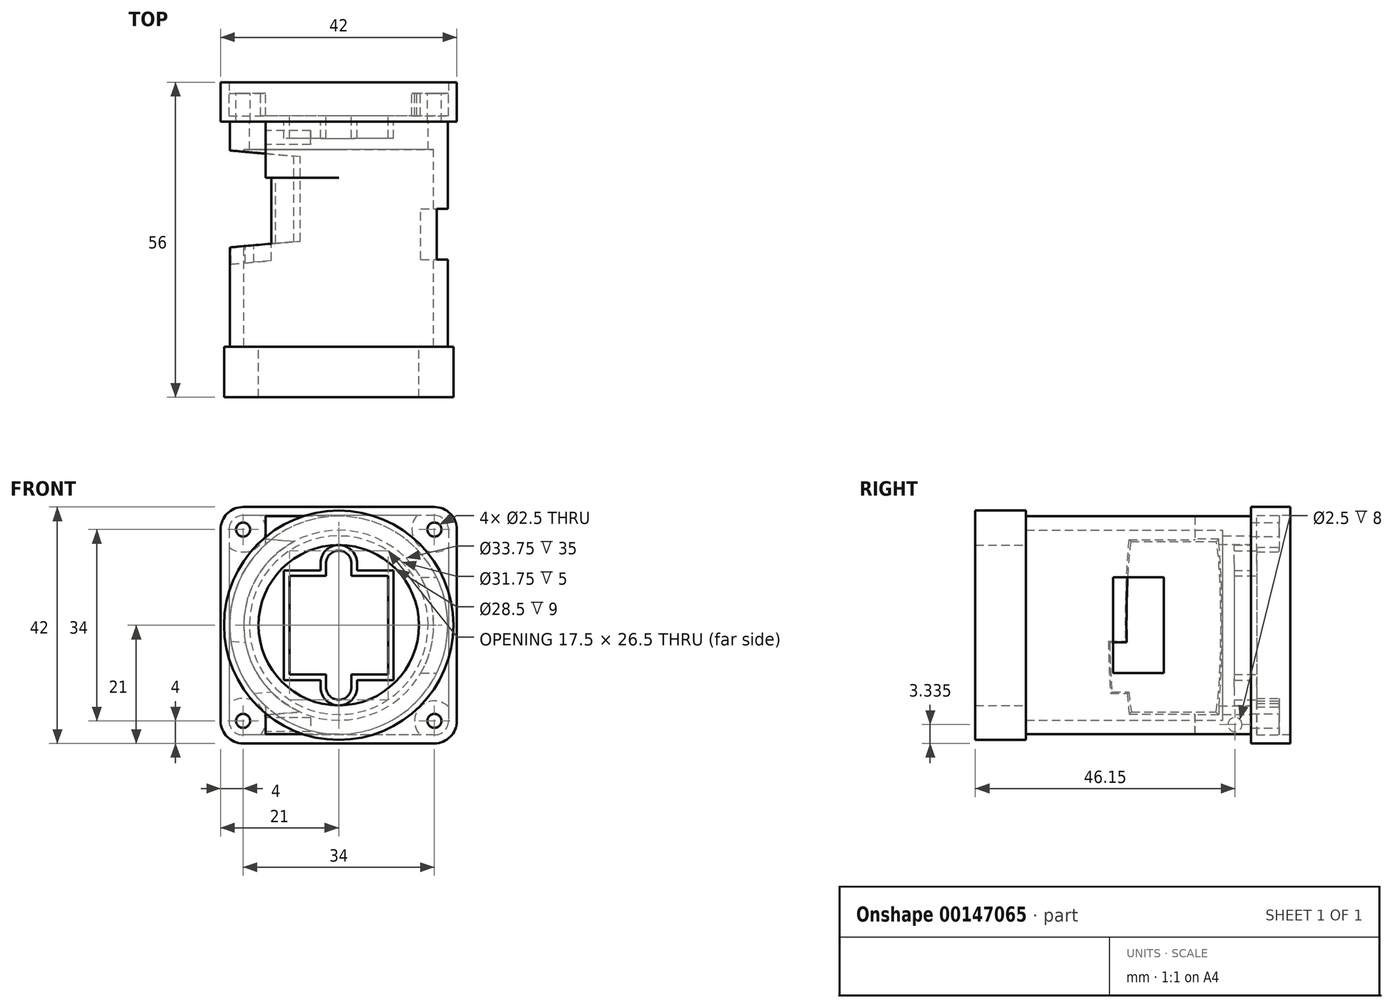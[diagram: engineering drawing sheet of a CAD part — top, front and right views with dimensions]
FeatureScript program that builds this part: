
annotation { "Feature Type Name" : "Feature", "Feature Type Description" : "" }
export const myFeature = defineFeature(function(context is Context, id is Id, definition is map)
    precondition{}
    {
        {
            var Q0;
            Q0=qCreatedBy(makeId("Front.planeOp"),FACE);
            var sketch = newSketch(context, id + "F0", { "sketchPlane" : qUnion([Q0])});
            skLineSegment(sketch, "E0.bottom", {"start": v(17, 19.5) * mm, "end": v(-17, 19.5) * mm});
            skLineSegment(sketch, "E0.top", {"start": v(17, -19.5) * mm, "end": v(-17, -19.5) * mm});
            skLineSegment(sketch, "E0.left", {"start": v(19.5, 17) * mm, "end": v(19.5, -17) * mm});
            skLineSegment(sketch, "E0.right", {"start": v(-19.5, 17) * mm, "end": v(-19.5, -17) * mm});
            skPoint(sketch, "E0.middle", {"position": v(0, 0) * mm});
            skPoint(sketch, "E1.visualSharp", {"position": v(-19.5, 19.5) * mm});
            skArc(sketch, "E1.filletArc", {"start": v(-17, 19.5) * mm, "mid": v(-18.77, 18.77) * mm, "end": v(-19.5, 17) * mm});
            skPoint(sketch, "E2.visualSharp", {"position": v(19.5, 19.5) * mm});
            skArc(sketch, "E2.filletArc", {"start": v(19.5, 17) * mm, "mid": v(18.77, 18.77) * mm, "end": v(17, 19.5) * mm});
            skPoint(sketch, "E3.visualSharp", {"position": v(19.5, -19.5) * mm});
            skArc(sketch, "E3.filletArc", {"start": v(17, -19.5) * mm, "mid": v(18.77, -18.77) * mm, "end": v(19.5, -17) * mm});
            skPoint(sketch, "E4.visualSharp", {"position": v(-19.5, -19.5) * mm});
            skArc(sketch, "E4.filletArc", {"start": v(-19.5, -17) * mm, "mid": v(-18.77, -18.77) * mm, "end": v(-17, -19.5) * mm});
            skLineSegment(sketch, "E5.0", {"start": v(17, 21) * mm, "end": v(-17, 21) * mm});
            skArc(sketch, "E5.1", {"start": v(21, 17) * mm, "mid": v(19.83, 19.83) * mm, "end": v(17, 21) * mm});
            skArc(sketch, "E5.2", {"start": v(-17, 21) * mm, "mid": v(-19.83, 19.83) * mm, "end": v(-21, 17) * mm});
            skLineSegment(sketch, "E5.3", {"start": v(21, 17) * mm, "end": v(21, -17) * mm});
            skLineSegment(sketch, "E5.4", {"start": v(-21, 17) * mm, "end": v(-21, -17) * mm});
            skArc(sketch, "E5.5", {"start": v(-21, -17) * mm, "mid": v(-19.83, -19.83) * mm, "end": v(-17, -21) * mm});
            skLineSegment(sketch, "E5.6", {"start": v(17, -21) * mm, "end": v(-17, -21) * mm});
            skArc(sketch, "E5.7", {"start": v(17, -21) * mm, "mid": v(19.83, -19.83) * mm, "end": v(21, -17) * mm});
            skCircle(sketch, "E6", {"center": v(-17, 17) * mm, "radius": 1.25 * mm});
            skLineSegment(sketch, "E7", {"start": v(0, 21) * mm, "end": v(0, -21) * mm, "construction": true});
            skLineSegment(sketch, "E8", {"start": v(-21, 0) * mm, "end": v(21, 0) * mm, "construction": true});
            skCircle(sketch, "E9", {"center": v(17, 17) * mm, "radius": 1.25 * mm});
            skCircle(sketch, "E10", {"center": v(17, -17) * mm, "radius": 1.25 * mm});
            skCircle(sketch, "E11", {"center": v(-17, -17) * mm, "radius": 1.25 * mm});
            skCircle(sketch, "E12", {"center": v(-17, 17) * mm, "radius": 4 * mm});
            skCircle(sketch, "E13", {"center": v(17, 17) * mm, "radius": 4 * mm});
            skCircle(sketch, "E14", {"center": v(17, -17) * mm, "radius": 3.54 * mm});
            skCircle(sketch, "E15", {"center": v(-17, -17) * mm, "radius": 4 * mm});
            skSolve(sketch);
        }
        {
            var Q0;
            {var subQ0=sQuery(id+"F0.wireOp",EDGE,"E1.filletArc");Q0=makeQuery(id+"F0.imprint","IMPRINT",FACE,{"disambiguationData":[TD([[makeQuery(id+"F0.imprint","IMPRINT",EDGE,{"derivedFrom":subQ0}),1.0]])]});}
            var Q1;
            {var subQ0=sQuery(id+"F0.wireOp",EDGE,"E2.filletArc");Q1=makeQuery(id+"F0.imprint","IMPRINT",FACE,{"disambiguationData":[TD([[makeQuery(id+"F0.imprint","IMPRINT",EDGE,{"derivedFrom":subQ0}),1.0]])]});}
            var Q2;
            {var subQ0=sQuery(id+"F0.wireOp",EDGE,"E3.filletArc");Q2=makeQuery(id+"F0.imprint","IMPRINT",FACE,{"disambiguationData":[TD([[makeQuery(id+"F0.imprint","IMPRINT",EDGE,{"derivedFrom":subQ0}),1.0]])]});}
            var Q3;
            {var subQ0=sQuery(id+"F0.wireOp",EDGE,"E4.filletArc");Q3=makeQuery(id+"F0.imprint","IMPRINT",FACE,{"disambiguationData":[TD([[makeQuery(id+"F0.imprint","IMPRINT",EDGE,{"derivedFrom":subQ0}),1.0]])]});}
            var Q4;
            {var subQ5=sQuery(id+"F0.wireOp",EDGE,"E5.4");Q4=makeQuery(id+"F0.imprint","IMPRINT",FACE,{"disambiguationData":[TD([[makeQuery(id+"F0.imprint","IMPRINT",EDGE,{"derivedFrom":subQ5}),1.0]])]});}
            var Q5;
            {var subQ0=sQuery(id+"F0.wireOp",EDGE,"E14");var subQ1=sQuery(id+"F0.wireOp",EDGE,"E0.top");var subQ2=makeQuery(id+"F0.imprint","INTERSECT",VERTEX,{"derivedFrom":[subQ1,subQ0]});Q5=makeQuery(id+"F0.imprint","IMPRINT",FACE,{"disambiguationData":[TD([[makeQuery(id+"F0.imprint","IMPRINT",EDGE,{"disambiguationData":[TD([[subQ2,-1.0]])],"derivedFrom":subQ1}),1.0]])]});}
            var Q6;
            {var subQ4=sQuery(id+"F0.wireOp",EDGE,"E1.filletArc");Q6=makeQuery(id+"F0.imprint","IMPRINT",FACE,{"disambiguationData":[TD([[makeQuery(id+"F0.imprint","IMPRINT",EDGE,{"derivedFrom":subQ4}),-1.0]])]});}
            var Q7;
            {var subQ5=sQuery(id+"F0.wireOp",EDGE,"E5.0");Q7=makeQuery(id+"F0.imprint","IMPRINT",FACE,{"disambiguationData":[TD([[makeQuery(id+"F0.imprint","IMPRINT",EDGE,{"derivedFrom":subQ5}),1.0]])]});}
            var Q8;
            {var subQ3=sQuery(id+"F0.wireOp",EDGE,"E2.filletArc");Q8=makeQuery(id+"F0.imprint","IMPRINT",FACE,{"disambiguationData":[TD([[makeQuery(id+"F0.imprint","IMPRINT",EDGE,{"derivedFrom":subQ3}),-1.0]])]});}
            var Q9;
            {var subQ0=sQuery(id+"F0.wireOp",EDGE,"E13");var subQ1=sQuery(id+"F0.wireOp",EDGE,"E0.left");var subQ2=makeQuery(id+"F0.imprint","INTERSECT",VERTEX,{"derivedFrom":[subQ1,subQ0]});Q9=makeQuery(id+"F0.imprint","IMPRINT",FACE,{"disambiguationData":[TD([[makeQuery(id+"F0.imprint","IMPRINT",EDGE,{"disambiguationData":[TD([[subQ2,-1.0]])],"derivedFrom":subQ1}),1.0]])]});}
            var Q10;
            {var subQ0=sQuery(id+"F0.wireOp",EDGE,"E3.filletArc");Q10=makeQuery(id+"F0.imprint","IMPRINT",FACE,{"disambiguationData":[TD([[makeQuery(id+"F0.imprint","IMPRINT",EDGE,{"derivedFrom":subQ0}),-1.0]])]});}
            var Q11;
            {var subQ4=sQuery(id+"F0.wireOp",EDGE,"E4.filletArc");Q11=makeQuery(id+"F0.imprint","IMPRINT",FACE,{"disambiguationData":[TD([[makeQuery(id+"F0.imprint","IMPRINT",EDGE,{"derivedFrom":subQ4}),-1.0]])]});}
            extrude(context, id + "F1", {"entities" : qUnion([Q0, Q1, Q2, Q3, Q4, Q5, Q6, Q7, Q8, Q9, Q10, Q11]), "depth" : 4 * mm});
        }
        {
            var Q0;
            {var subQ5=sQuery(id+"F0.wireOp",EDGE,"E5.0");Q0=makeQuery(id+"F0.imprint","IMPRINT",FACE,{"disambiguationData":[TD([[makeQuery(id+"F0.imprint","IMPRINT",EDGE,{"derivedFrom":subQ5}),1.0]])]});}
            var Q1;
            {var subQ3=sQuery(id+"F0.wireOp",EDGE,"E2.filletArc");Q1=makeQuery(id+"F0.imprint","IMPRINT",FACE,{"disambiguationData":[TD([[makeQuery(id+"F0.imprint","IMPRINT",EDGE,{"derivedFrom":subQ3}),-1.0]])]});}
            var Q2;
            {var subQ4=sQuery(id+"F0.wireOp",EDGE,"E1.filletArc");Q2=makeQuery(id+"F0.imprint","IMPRINT",FACE,{"disambiguationData":[TD([[makeQuery(id+"F0.imprint","IMPRINT",EDGE,{"derivedFrom":subQ4}),-1.0]])]});}
            var Q3;
            {var subQ5=sQuery(id+"F0.wireOp",EDGE,"E5.4");Q3=makeQuery(id+"F0.imprint","IMPRINT",FACE,{"disambiguationData":[TD([[makeQuery(id+"F0.imprint","IMPRINT",EDGE,{"derivedFrom":subQ5}),1.0]])]});}
            var Q4;
            {var subQ4=sQuery(id+"F0.wireOp",EDGE,"E4.filletArc");Q4=makeQuery(id+"F0.imprint","IMPRINT",FACE,{"disambiguationData":[TD([[makeQuery(id+"F0.imprint","IMPRINT",EDGE,{"derivedFrom":subQ4}),-1.0]])]});}
            var Q5;
            {var subQ0=sQuery(id+"F0.wireOp",EDGE,"E14");var subQ1=sQuery(id+"F0.wireOp",EDGE,"E0.top");var subQ2=makeQuery(id+"F0.imprint","INTERSECT",VERTEX,{"derivedFrom":[subQ1,subQ0]});Q5=makeQuery(id+"F0.imprint","IMPRINT",FACE,{"disambiguationData":[TD([[makeQuery(id+"F0.imprint","IMPRINT",EDGE,{"disambiguationData":[TD([[subQ2,-1.0]])],"derivedFrom":subQ1}),1.0]])]});}
            var Q6;
            {var subQ0=sQuery(id+"F0.wireOp",EDGE,"E3.filletArc");Q6=makeQuery(id+"F0.imprint","IMPRINT",FACE,{"disambiguationData":[TD([[makeQuery(id+"F0.imprint","IMPRINT",EDGE,{"derivedFrom":subQ0}),-1.0]])]});}
            var Q7;
            {var subQ0=sQuery(id+"F0.wireOp",EDGE,"E13");var subQ1=sQuery(id+"F0.wireOp",EDGE,"E0.left");var subQ2=makeQuery(id+"F0.imprint","INTERSECT",VERTEX,{"derivedFrom":[subQ1,subQ0]});Q7=makeQuery(id+"F0.imprint","IMPRINT",FACE,{"disambiguationData":[TD([[makeQuery(id+"F0.imprint","IMPRINT",EDGE,{"disambiguationData":[TD([[subQ2,-1.0]])],"derivedFrom":subQ1}),1.0]])]});}
            extrude(context, id + "F2", {"entities" : qUnion([Q0, Q1, Q2, Q3, Q4, Q5, Q6, Q7]), "operationType" : NewBodyOperationType.ADD, "oppositeDirection" : true, "depth" : 2 * mm});
        }
        {
            var Q0;
            Q0=makeQuery(id+"F1.opExtrude","CAP_FACE",FACE,{"disambiguationData":[OSD([sQuery(id+"F0.wireOp",EDGE,"E0.bottom"),sQuery(id+"F0.wireOp",EDGE,"E0.top"),sQuery(id+"F0.wireOp",EDGE,"E0.left"),sQuery(id+"F0.wireOp",EDGE,"E0.right"),sQuery(id+"F0.wireOp",EDGE,"E5.0"),sQuery(id+"F0.wireOp",EDGE,"E5.3"),sQuery(id+"F0.wireOp",EDGE,"E5.4"),sQuery(id+"F0.wireOp",EDGE,"E5.6"),sQuery(id+"F0.wireOp",EDGE,"E5.7"),sQuery(id+"F0.wireOp",EDGE,"E6"),sQuery(id+"F0.wireOp",EDGE,"E9"),sQuery(id+"F0.wireOp",EDGE,"E10"),sQuery(id+"F0.wireOp",EDGE,"E11"),sQuery(id+"F0.wireOp",EDGE,"E12"),sQuery(id+"F0.wireOp",EDGE,"E13"),sQuery(id+"F0.wireOp",EDGE,"E14"),sQuery(id+"F0.wireOp",EDGE,"E15")])],"isStart":false});
            var sketch = newSketch(context, id + "F3", { "sketchPlane" : qUnion([Q0])});
            skArc(sketch, "E16.0", {"start": v(-17, 21) * mm, "mid": v(-19.83, 19.83) * mm, "end": v(-21, 17) * mm});
            skLineSegment(sketch, "E16.1", {"start": v(17, 21) * mm, "end": v(-17, 21) * mm});
            skLineSegment(sketch, "E16.2", {"start": v(-21, 17) * mm, "end": v(-21, -17) * mm});
            skArc(sketch, "E16.3", {"start": v(-21, -17) * mm, "mid": v(-19.83, -19.83) * mm, "end": v(-17, -21) * mm});
            skLineSegment(sketch, "E16.4", {"start": v(17, -21) * mm, "end": v(-17, -21) * mm});
            skArc(sketch, "E16.5", {"start": v(17, -21) * mm, "mid": v(19.83, -19.83) * mm, "end": v(21, -17) * mm});
            skLineSegment(sketch, "E16.6", {"start": v(21, 17) * mm, "end": v(21, -17) * mm});
            skArc(sketch, "E16.7", {"start": v(21, 17) * mm, "mid": v(19.83, 19.83) * mm, "end": v(17, 21) * mm});
            skLineSegment(sketch, "E17.0", {"start": v(-21, 0) * mm, "end": v(21, 0) * mm, "construction": true});
            skLineSegment(sketch, "E17.1", {"start": v(0, 21) * mm, "end": v(0, -21) * mm, "construction": true});
            skLineSegment(sketch, "E18.bottom", {"start": v(8.75, 8.75) * mm, "end": v(2.25, 8.75) * mm});
            skLineSegment(sketch, "E18.top", {"start": v(8.75, -8.75) * mm, "end": v(2.25, -8.75) * mm});
            skLineSegment(sketch, "E18.left", {"start": v(8.75, 8.75) * mm, "end": v(8.75, -8.75) * mm});
            skLineSegment(sketch, "E18.right", {"start": v(-8.75, 8.75) * mm, "end": v(-8.75, -8.75) * mm});
            skPoint(sketch, "E18.middle", {"position": v(0, 0) * mm});
            skLineSegment(sketch, "E19.0", {"start": v(11, 11) * mm, "end": v(-11, 11) * mm, "construction": true});
            skLineSegment(sketch, "E19.1", {"start": v(11, 11) * mm, "end": v(11, -11) * mm, "construction": true});
            skLineSegment(sketch, "E19.2", {"start": v(11, -11) * mm, "end": v(-11, -11) * mm, "construction": true});
            skLineSegment(sketch, "E19.3", {"start": v(-11, 11) * mm, "end": v(-11, -11) * mm, "construction": true});
            skArc(sketch, "E20", {"start": v(-2.25, 11) * mm, "mid": v(0, 13.25) * mm, "end": v(2.25, 11) * mm});
            skLineSegment(sketch, "E21", {"start": v(-2.25, 11) * mm, "end": v(-2.25, 8.75) * mm});
            skLineSegment(sketch, "E22", {"start": v(2.25, 11) * mm, "end": v(2.25, 8.75) * mm});
            skLineSegment(sketch, "E23.trimOffspring", {"start": v(-2.25, 8.75) * mm, "end": v(-8.75, 8.75) * mm});
            skLineSegment(sketch, "E24.MirrorCS", {"start": v(-2.25, -11) * mm, "end": v(-2.25, -8.75) * mm});
            skLineSegment(sketch, "E25.MirrorCS", {"start": v(2.25, -11) * mm, "end": v(2.25, -8.75) * mm});
            skArc(sketch, "E26.MirrorCS", {"start": v(-2.25, -11) * mm, "mid": v(0, -13.25) * mm, "end": v(2.25, -11) * mm});
            skLineSegment(sketch, "E27.trimOffspring", {"start": v(-2.25, -8.75) * mm, "end": v(-8.75, -8.75) * mm});
            skArc(sketch, "E28.0", {"start": v(-3.25, -11) * mm, "mid": v(0, -14.25) * mm, "end": v(3.25, -11) * mm});
            skLineSegment(sketch, "E28.1", {"start": v(-3.25, 11) * mm, "end": v(-3.25, 9.75) * mm});
            skLineSegment(sketch, "E28.2", {"start": v(-3.25, 9.75) * mm, "end": v(-9.75, 9.75) * mm});
            skLineSegment(sketch, "E28.3", {"start": v(-9.75, 9.75) * mm, "end": v(-9.75, -9.75) * mm});
            skLineSegment(sketch, "E28.4", {"start": v(-3.25, -9.75) * mm, "end": v(-9.75, -9.75) * mm});
            skArc(sketch, "E28.5", {"start": v(-3.25, 11) * mm, "mid": v(0, 14.25) * mm, "end": v(3.25, 11) * mm});
            skLineSegment(sketch, "E28.6", {"start": v(-3.25, -11) * mm, "end": v(-3.25, -9.75) * mm});
            skLineSegment(sketch, "E28.7", {"start": v(3.25, 11) * mm, "end": v(3.25, 9.75) * mm});
            skLineSegment(sketch, "E28.8", {"start": v(9.75, 9.75) * mm, "end": v(3.25, 9.75) * mm});
            skLineSegment(sketch, "E28.9", {"start": v(9.75, 9.75) * mm, "end": v(9.75, -9.75) * mm});
            skLineSegment(sketch, "E28.10", {"start": v(9.75, -9.75) * mm, "end": v(3.25, -9.75) * mm});
            skLineSegment(sketch, "E28.11", {"start": v(3.25, -11) * mm, "end": v(3.25, -9.75) * mm});
            skSolve(sketch);
        }
        {
            var Q0;
            Q0=makeQuery(id+"F3.imprint","IMPRINT",FACE,{"disambiguationData":[TD([[makeQuery(id+"F3.imprint","IMPRINT",EDGE,{"derivedFrom":sQuery(id+"F3.wireOp",EDGE,"E16.0")}),1.0]])]});
            var Q1;
            Q1=makeQuery(id+"F3.imprint","IMPRINT",FACE,{"disambiguationData":[TD([[makeQuery(id+"F3.imprint","IMPRINT",EDGE,{"derivedFrom":sQuery(id+"F3.wireOp",EDGE,"E28.0")}),-1.0]])]});
            var Q2;
            Q2=makeQuery(id+"F3.imprint","IMPRINT",FACE,{"disambiguationData":[TD([[makeQuery(id+"F3.imprint","IMPRINT",EDGE,{"derivedFrom":sQuery(id+"F3.wireOp",EDGE,"E18.bottom")}),-1.0]])]});
            extrude(context, id + "F4", {"entities" : qUnion([Q0, Q1, Q2]), "operationType" : NewBodyOperationType.ADD, "depth" : 1 * mm, "offsetDistance" : 25 * mm});
        }
        {
            var Q0;
            Q0=makeQuery(id+"F3.imprint","IMPRINT",FACE,{"disambiguationData":[TD([[makeQuery(id+"F3.imprint","IMPRINT",EDGE,{"derivedFrom":sQuery(id+"F3.wireOp",EDGE,"E18.bottom")}),-1.0]])]});
            extrude(context, id + "F5", {"entities" : qUnion([Q0]), "operationType" : NewBodyOperationType.ADD, "depth" : 4 * mm, "offsetDistance" : 25 * mm});
        }
        {
            var Q0;
            Q0=makeQuery(id+"F4.opExtrude","CAP_FACE",FACE,{"disambiguationData":[OSD([sQuery(id+"F0.wireOp",EDGE,"E6"),sQuery(id+"F0.wireOp",EDGE,"E9"),sQuery(id+"F0.wireOp",EDGE,"E10"),sQuery(id+"F0.wireOp",EDGE,"E11"),sQuery(id+"F3.wireOp",EDGE,"E16.0"),sQuery(id+"F3.wireOp",EDGE,"E16.1"),sQuery(id+"F3.wireOp",EDGE,"E16.2"),sQuery(id+"F3.wireOp",EDGE,"E16.3"),sQuery(id+"F3.wireOp",EDGE,"E16.4"),sQuery(id+"F3.wireOp",EDGE,"E16.5"),sQuery(id+"F3.wireOp",EDGE,"E16.6"),sQuery(id+"F3.wireOp",EDGE,"E16.7"),sQuery(id+"F3.wireOp",EDGE,"E18.bottom"),sQuery(id+"F3.wireOp",EDGE,"E18.top"),sQuery(id+"F3.wireOp",EDGE,"E18.left"),sQuery(id+"F3.wireOp",EDGE,"E18.right"),sQuery(id+"F3.wireOp",EDGE,"E20"),sQuery(id+"F3.wireOp",EDGE,"E21"),sQuery(id+"F3.wireOp",EDGE,"E22"),sQuery(id+"F3.wireOp",EDGE,"E23.trimOffspring"),sQuery(id+"F3.wireOp",EDGE,"E24.MirrorCS"),sQuery(id+"F3.wireOp",EDGE,"E25.MirrorCS"),sQuery(id+"F3.wireOp",EDGE,"E26.MirrorCS"),sQuery(id+"F3.wireOp",EDGE,"E27.trimOffspring")])],"isStart":false});
            var sketch = newSketch(context, id + "F6", { "sketchPlane" : qUnion([Q0])});
            skCircle(sketch, "E29", {"center": v(0, 0) * mm, "radius": 19.38 * mm});
            skCircle(sketch, "E30.0", {"center": v(0, 0) * mm, "radius": 16.88 * mm});
            skCircle(sketch, "E31.0", {"center": v(0, 0) * mm, "radius": 15.88 * mm});
            skLineSegment(sketch, "E32", {"start": v(0, -19.38) * mm, "end": v(-10.75, -19.38) * mm});
            skLineSegment(sketch, "E33", {"start": v(-10.75, -19.38) * mm, "end": v(-10.75, -13) * mm});
            skLineSegment(sketch, "E34.MirrorCS", {"start": v(0, 19.38) * mm, "end": v(-10.75, 19.38) * mm});
            skLineSegment(sketch, "E35.MirrorCS", {"start": v(-10.75, 19.38) * mm, "end": v(-10.75, 13) * mm});
            skLineSegment(sketch, "E36", {"start": v(-10.75, -19.38) * mm, "end": v(-13, -19.38) * mm});
            skLineSegment(sketch, "E37", {"start": v(-13, -19.37) * mm, "end": v(-13, -10.76) * mm});
            skLineSegment(sketch, "E38.MirrorCS", {"start": v(-10.75, 19.38) * mm, "end": v(-13, 19.38) * mm});
            skLineSegment(sketch, "E39.MirrorCS", {"start": v(-13, 19.38) * mm, "end": v(-13, 10.76) * mm});
            skSolve(sketch);
        }
        {
            var Q0;
            {var subQ5=sQuery(id+"F6.wireOp",EDGE,"E29");var subQ6=makeQuery(id+"F6.imprint","INTERSECT",VERTEX,{"derivedFrom":[subQ5,sQuery(id+"F6.wireOp",EDGE,"E32")]});Q0=makeQuery(id+"F6.imprint","IMPRINT",FACE,{"disambiguationData":[TD([[makeQuery(id+"F6.imprint","IMPRINT",EDGE,{"disambiguationData":[TD([[subQ6,1.0]])],"derivedFrom":subQ5}),1.0]])]});}
            extrude(context, id + "F7", {"entities" : qUnion([Q0]), "depth" : 48 * mm});
        }
        {
            var Q0;
            {var subQ0=sQuery(id+"F6.wireOp",EDGE,"E37");var subQ1=sQuery(id+"F6.wireOp",EDGE,"E29");var subQ2=makeQuery(id+"F6.imprint","INTERSECT",VERTEX,{"derivedFrom":[subQ1,subQ0]});Q0=makeQuery(id+"F6.imprint","IMPRINT",FACE,{"disambiguationData":[TD([[makeQuery(id+"F6.imprint","IMPRINT",EDGE,{"disambiguationData":[TD([[subQ2,1.0]])],"derivedFrom":subQ1}),1.0]])]});}
            var Q1;
            {var subQ0=sQuery(id+"F6.wireOp",EDGE,"E33");var subQ1=sQuery(id+"F6.wireOp",EDGE,"E29");var subQ2=makeQuery(id+"F6.imprint","INTERSECT",VERTEX,{"derivedFrom":[subQ1,subQ0]});Q1=makeQuery(id+"F6.imprint","IMPRINT",FACE,{"disambiguationData":[TD([[makeQuery(id+"F6.imprint","IMPRINT",EDGE,{"disambiguationData":[TD([[subQ2,1.0]])],"derivedFrom":subQ1}),1.0]])]});}
            var Q2;
            {var subQ0=sQuery(id+"F6.wireOp",EDGE,"E35.MirrorCS");var subQ1=sQuery(id+"F6.wireOp",EDGE,"E29");var subQ2=makeQuery(id+"F6.imprint","INTERSECT",VERTEX,{"derivedFrom":[subQ1,subQ0]});Q2=makeQuery(id+"F6.imprint","IMPRINT",FACE,{"disambiguationData":[TD([[makeQuery(id+"F6.imprint","IMPRINT",EDGE,{"disambiguationData":[TD([[subQ2,-1.0]])],"derivedFrom":subQ1}),1.0]])]});}
            extrude(context, id + "F8", {"entities" : qUnion([Q0, Q1, Q2]), "depth" : 48 * mm});
        }
        {
            var Q0;
            {var subQ0=sQuery(id+"F6.wireOp",EDGE,"E32");Q0=makeQuery(id+"F6.imprint","IMPRINT",FACE,{"disambiguationData":[TD([[makeQuery(id+"F6.imprint","IMPRINT",EDGE,{"derivedFrom":subQ0}),-1.0]])]});}
            var Q1;
            {var subQ0=sQuery(id+"F6.wireOp",EDGE,"E34.MirrorCS");Q1=makeQuery(id+"F6.imprint","IMPRINT",FACE,{"disambiguationData":[TD([[makeQuery(id+"F6.imprint","IMPRINT",EDGE,{"derivedFrom":subQ0}),1.0]])]});}
            extrude(context, id + "F9", {"entities" : qUnion([Q0, Q1]), "operationType" : NewBodyOperationType.ADD, "depth" : 10 * mm});
        }
        {
            var Q0;
            {var subQ5=sQuery(id+"F6.wireOp",EDGE,"E36");Q0=makeQuery(id+"F6.imprint","IMPRINT",FACE,{"disambiguationData":[TD([[makeQuery(id+"F6.imprint","IMPRINT",EDGE,{"derivedFrom":subQ5}),-1.0]])]});}
            var Q1;
            {var subQ5=sQuery(id+"F6.wireOp",EDGE,"E38.MirrorCS");Q1=makeQuery(id+"F6.imprint","IMPRINT",FACE,{"disambiguationData":[TD([[makeQuery(id+"F6.imprint","IMPRINT",EDGE,{"derivedFrom":subQ5}),1.0]])]});}
            extrude(context, id + "F10", {"entities" : qUnion([Q0, Q1]), "operationType" : NewBodyOperationType.ADD, "depth" : 10 * mm});
        }
        {
            var Q0;
            Q0=makeQuery(id+"F6.imprint","IMPRINT",FACE,{"disambiguationData":[TD([[makeQuery(id+"F6.imprint","IMPRINT",EDGE,{"derivedFrom":sQuery(id+"F6.wireOp",EDGE,"E31.0")}),-1.0]])]});
            extrude(context, id + "F11", {"entities" : qUnion([Q0]), "operationType" : NewBodyOperationType.ADD, "depth" : 5 * mm});
        }
        {
            var Q0;
            {var subQ0=sQuery(id+"F0.wireOp",EDGE,"E5.3");Q0=makeQuery(id+"F4.boolean.opBoolean","MERGE",FACE,{"derivedFrom":[makeQuery(id+"F2.boolean.opBoolean","MERGE",FACE,{"derivedFrom":[makeQuery(id+"F1.opExtrude","SWEPT_FACE",FACE,{"disambiguationData":[OSD([subQ0])]}),makeQuery(id+"F2.opExtrude","SWEPT_FACE",FACE,{"disambiguationData":[OSD([subQ0])]})]}),makeQuery(id+"F4.opExtrude","SWEPT_FACE",FACE,{"disambiguationData":[OSD([sQuery(id+"F3.wireOp",EDGE,"E16.6")])]})]});}
            var sketch = newSketch(context, id + "F12", { "sketchPlane" : qUnion([Q0])});
            skPoint(sketch, "E40.middle", {"position": v(-18.75, 0) * mm});
            skLineSegment(sketch, "E41", {"start": v(-20.5, 27.44) * mm, "end": v(-20.5, -22.27) * mm, "construction": true});
            skLineSegment(sketch, "E42", {"start": v(-29.5, 27.44) * mm, "end": v(-29.5, -21.95) * mm, "construction": true});
            skLineSegment(sketch, "E43", {"start": v(-29.5, 0) * mm, "end": v(-20.5, 0) * mm, "construction": true});
            skLineSegment(sketch, "E44.bottom", {"start": v(-20.5, 8.5) * mm, "end": v(-29.5, 8.5) * mm});
            skLineSegment(sketch, "E44.top", {"start": v(-20.5, -8.5) * mm, "end": v(-29.5, -8.5) * mm});
            skLineSegment(sketch, "E44.left", {"start": v(-20.5, 8.5) * mm, "end": v(-20.5, -8.5) * mm});
            skLineSegment(sketch, "E44.right", {"start": v(-29.5, 8.5) * mm, "end": v(-29.5, -8.5) * mm});
            skPoint(sketch, "E44.middle", {"position": v(-25, 0) * mm});
            skSolve(sketch);
        }
        {
            var Q0;
            {var subQ0=sQuery(id+"F0.wireOp",EDGE,"E5.4");Q0=makeQuery(id+"F4.boolean.opBoolean","MERGE",FACE,{"derivedFrom":[makeQuery(id+"F2.boolean.opBoolean","MERGE",FACE,{"derivedFrom":[makeQuery(id+"F1.opExtrude","SWEPT_FACE",FACE,{"disambiguationData":[OSD([subQ0])]}),makeQuery(id+"F2.opExtrude","SWEPT_FACE",FACE,{"disambiguationData":[OSD([subQ0])]})]}),makeQuery(id+"F4.opExtrude","SWEPT_FACE",FACE,{"disambiguationData":[OSD([sQuery(id+"F3.wireOp",EDGE,"E16.2")])]})]});}
            var sketch = newSketch(context, id + "F13", { "sketchPlane" : qUnion([Q0])});
            skLineSegment(sketch, "E45.0", {"start": v(10, 16) * mm, "end": v(10, -16) * mm});
            skLineSegment(sketch, "E45.1", {"start": v(10, 16) * mm, "end": v(27.5, 16) * mm});
            skLineSegment(sketch, "E45.2", {"start": v(27.5, 15.34) * mm, "end": v(27.5, -16.66) * mm});
            skLineSegment(sketch, "E45.3", {"start": v(10, -16.66) * mm, "end": v(27.5, -16.66) * mm});
            skLineSegment(sketch, "E45.4", {"start": v(27.5, 0) * mm, "end": v(10, 0) * mm});
            skLineSegment(sketch, "E45.5", {"start": v(10, 20.73) * mm, "end": v(10, -20.73) * mm});
            skLineSegment(sketch, "E45.6", {"start": v(27.5, 20.73) * mm, "end": v(27.5, -20.73) * mm});
            skLineSegment(sketch, "E46.bottom", {"start": v(27.5, -12.66) * mm, "end": v(30.5, -12.66) * mm});
            skLineSegment(sketch, "E46.top", {"start": v(27.5, -2.66) * mm, "end": v(30.5, -2.66) * mm});
            skLineSegment(sketch, "E46.left", {"start": v(27.5, -12.66) * mm, "end": v(27.5, -2.66) * mm});
            skLineSegment(sketch, "E46.right", {"start": v(30.5, -12.66) * mm, "end": v(30.5, -2.66) * mm});
            skSolve(sketch);
        }
        {
            var Q0;
            {var subQ0=sQuery(id+"F13.wireOp",EDGE,"E45.1");Q0=makeQuery(id+"F13.imprint","IMPRINT",FACE,{"disambiguationData":[TD([[makeQuery(id+"F13.imprint","IMPRINT",EDGE,{"derivedFrom":subQ0}),-1.0]])]});}
            var Q1;
            {var subQ0=sQuery(id+"F13.wireOp",EDGE,"E45.3");Q1=makeQuery(id+"F13.imprint","IMPRINT",FACE,{"disambiguationData":[TD([[makeQuery(id+"F13.imprint","IMPRINT",EDGE,{"derivedFrom":subQ0}),1.0]])]});}
            var Q2;
            Q2=makeQuery(id+"F13.imprint","IMPRINT",FACE,{"disambiguationData":[TD([[makeQuery(id+"F13.imprint","IMPRINT",EDGE,{"derivedFrom":sQuery(id+"F13.wireOp",EDGE,"E46.bottom")}),1.0]])]});
            extrude(context, id + "F14", {"entities" : qUnion([Q0, Q1, Q2]), "operationType" : NewBodyOperationType.REMOVE, "oppositeDirection" : true, "depth" : 20 * mm, "hasDraft" : true, "draftAngle" : 5 * degree, "draftPullDirection" : true});
        }
        {
            var Q0;
            {var subQ5=sQuery(id+"F12.wireOp",EDGE,"E44.right");Q0=makeQuery(id+"F12.imprint","IMPRINT",FACE,{"disambiguationData":[TD([[makeQuery(id+"F12.imprint","IMPRINT",EDGE,{"derivedFrom":subQ5}),1.0]])]});}
            var Q1;
            {var subQ5=sQuery(id+"F12.wireOp",EDGE,"E44.left");Q1=makeQuery(id+"F12.imprint","IMPRINT",FACE,{"disambiguationData":[TD([[makeQuery(id+"F12.imprint","IMPRINT",EDGE,{"derivedFrom":subQ5}),-1.0]])]});}
            extrude(context, id + "F15", {"entities" : qUnion([Q0, Q1]), "operationType" : NewBodyOperationType.REMOVE, "oppositeDirection" : true, "depth" : 25 * mm});
        }
        {
            var Q0;
            Q0=makeQuery(id+"F7.opExtrude","CAP_FACE",FACE,{"disambiguationData":[OSD([sQuery(id+"F6.wireOp",EDGE,"E29"),sQuery(id+"F6.wireOp",EDGE,"E30.0"),sQuery(id+"F6.wireOp",EDGE,"E33"),sQuery(id+"F6.wireOp",EDGE,"E35.MirrorCS")])],"isStart":false});
            var sketch = newSketch(context, id + "F16", { "sketchPlane" : qUnion([Q0])});
            skCircle(sketch, "E47", {"center": v(0, 0) * mm, "radius": 14.25 * mm});
            skArc(sketch, "E48.0", {"start": v(-10.75, -16.12) * mm, "mid": v(19.38, 0) * mm, "end": v(-10.75, 16.12) * mm});
            skArc(sketch, "E48.1", {"start": v(-10.75, 16.12) * mm, "mid": v(-19.37, 0) * mm, "end": v(-10.75, -16.12) * mm});
            skArc(sketch, "E48.2", {"start": v(-10.75, 13) * mm, "mid": v(-16.88, 0) * mm, "end": v(-10.75, -13) * mm});
            skArc(sketch, "E48.3", {"start": v(-10.75, -13) * mm, "mid": v(16.88, 0) * mm, "end": v(-10.75, 13) * mm});
            skArc(sketch, "E49.0", {"start": v(11.4, 16.88) * mm, "mid": v(-20.38, 0) * mm, "end": v(11.4, -16.88) * mm});
            skArc(sketch, "E49.1", {"start": v(11.4, -16.88) * mm, "mid": v(20.38, 0) * mm, "end": v(11.4, 16.88) * mm});
            skSolve(sketch);
        }
        {
            var Q0;
            Q0=makeQuery(id+"F16.imprint","IMPRINT",FACE,{"disambiguationData":[TD([[makeQuery(id+"F16.imprint","IMPRINT",EDGE,{"derivedFrom":sQuery(id+"F16.wireOp",EDGE,"E47")}),-1.0]])]});
            var Q1;
            Q1=makeQuery(id+"F16.imprint","IMPRINT",FACE,{"disambiguationData":[TD([[makeQuery(id+"F16.imprint","IMPRINT",EDGE,{"derivedFrom":sQuery(id+"F16.wireOp",EDGE,"E48.0")}),1.0]])]});
            var Q2;
            Q2=makeQuery(id+"F16.imprint","IMPRINT",FACE,{"disambiguationData":[TD([[makeQuery(id+"F16.imprint","IMPRINT",EDGE,{"derivedFrom":sQuery(id+"F16.wireOp",EDGE,"E48.0")}),-1.0]])]});
            var Q3;
            Q3=makeQuery(id+"F16.imprint","IMPRINT",FACE,{"disambiguationData":[TD([[makeQuery(id+"F16.imprint","IMPRINT",EDGE,{"derivedFrom":sQuery(id+"F16.wireOp",EDGE,"E48.1")}),1.0]])]});
            extrude(context, id + "F17", {"entities" : qUnion([Q0, Q1, Q2, Q3]), "depth" : 1 * mm});
        }
        {
            var Q0;
            Q0=makeQuery(id+"F16.imprint","IMPRINT",FACE,{"disambiguationData":[TD([[makeQuery(id+"F16.imprint","IMPRINT",EDGE,{"derivedFrom":sQuery(id+"F16.wireOp",EDGE,"E48.0")}),-1.0]])]});
            var Q1;
            Q1=makeQuery(id+"F16.imprint","IMPRINT",FACE,{"disambiguationData":[TD([[makeQuery(id+"F16.imprint","IMPRINT",EDGE,{"derivedFrom":sQuery(id+"F16.wireOp",EDGE,"E47")}),-1.0]])]});
            extrude(context, id + "F18", {"entities" : qUnion([Q0, Q1]), "operationType" : NewBodyOperationType.ADD, "oppositeDirection" : true, "depth" : 8 * mm});
        }
        {
            var Q0;
            Q0=makeQuery(id+"F10.opExtrude","SWEPT_FACE",FACE,{"disambiguationData":[OSD([sQuery(id+"F6.wireOp",EDGE,"E37")])]});
            var sketch = newSketch(context, id + "F19", { "sketchPlane" : qUnion([Q0])});
            skCircle(sketch, "E50", {"center": v(7.85, -17.67) * mm, "radius": 1.25 * mm});
            skPoint(sketch, "E50.centerSnap0", {"position": v(15, -17.67) * mm});
            skPoint(sketch, "E50.centerSnap1", {"position": v(7.85, -14.37) * mm});
            skCircle(sketch, "E51.MirrorC", {"center": v(7.85, 17.67) * mm, "radius": 1.25 * mm});
            skSolve(sketch);
        }
        {
            var Q0;
            Q0=makeQuery(id+"F19.imprint","IMPRINT",FACE,{"disambiguationData":[TD([[makeQuery(id+"F19.imprint","IMPRINT",EDGE,{"derivedFrom":sQuery(id+"F19.wireOp",EDGE,"E50")}),1.0]])]});
            var Q1;
            Q1=makeQuery(id+"F19.imprint","IMPRINT",FACE,{"disambiguationData":[TD([[makeQuery(id+"F19.imprint","IMPRINT",EDGE,{"derivedFrom":sQuery(id+"F19.wireOp",EDGE,"E51.MirrorC")}),-1.0]])]});
            extrude(context, id + "F20", {"entities" : qUnion([Q0, Q1]), "operationType" : NewBodyOperationType.REMOVE, "oppositeDirection" : true, "depth" : 8 * mm});
        }
    });
